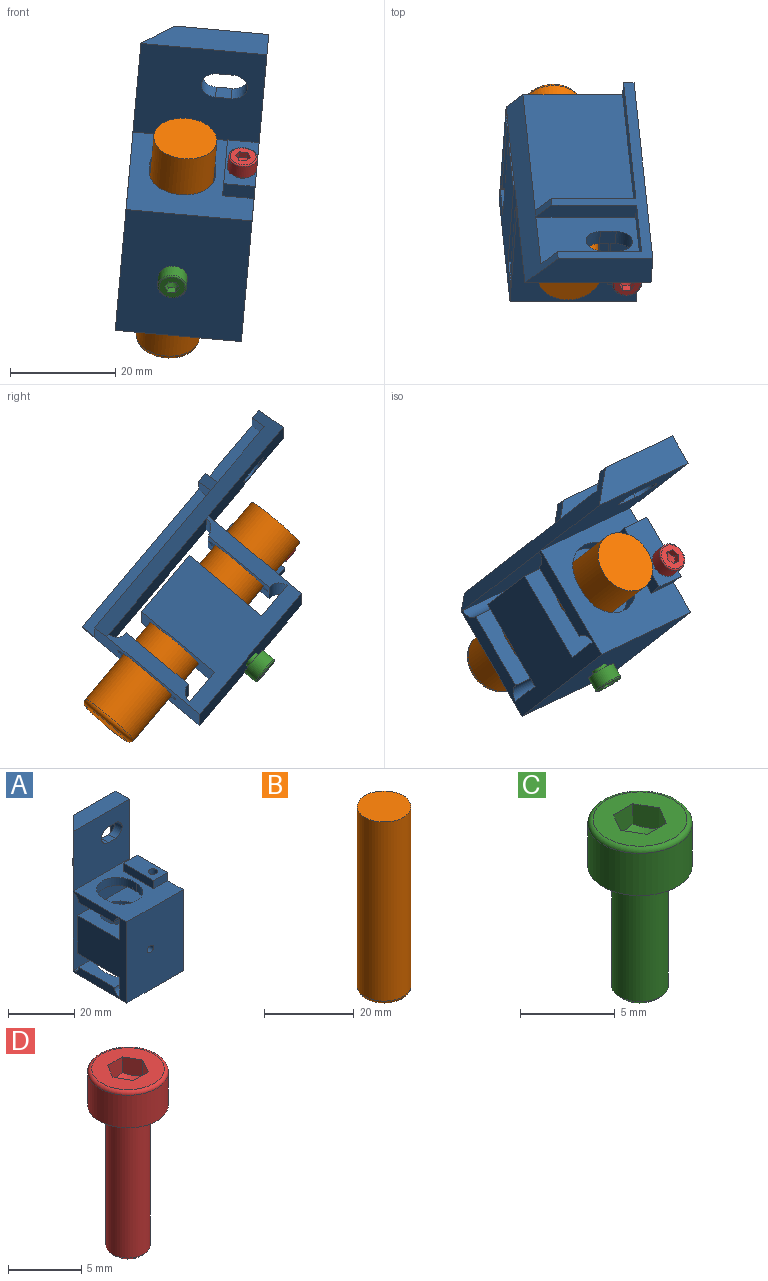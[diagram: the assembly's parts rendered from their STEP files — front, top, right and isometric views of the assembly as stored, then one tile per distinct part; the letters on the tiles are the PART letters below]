
ASSEMBLY  parts=4 mates=3
PART A: 61 faces, bbox 24x29x52 mm
  f0: plane 19x3mm, normal (0,0,-1), area 52.7mm2, adj f1,f11,f48,f58
  f1: plane 34.2x19mm, normal (0,1,0), area 649.8mm2, adj f0,f10,f48,f53
  f2: plane 13.8x3mm, normal (-1,0,0), area 41.4mm2, adj f6,f7,f11,f57
  f3: cylinder r=6.15mm len=3.53mm, axis (0,0,1), area 6.1mm2, adj f4,f46,f54,f59,f60
  f4: plane 9x7.5mm, normal (0,1,0), area 40.4mm2, adj f3,f13,f40,f45,f54,f55,f59
  f5: cylinder r=6.15mm len=14mm, axis (0,0,1), area 479.3mm2, adj f17,f19,f41,f42,f43,f44,f45,f56
  f6: plane 19x13.8mm, normal (0,1,0), area 218.4mm2, adj f2,f7,f49,f50,f51,f52,f53,f57
  f7: plane 19x3mm, normal (0,0,-1), area 52.5mm2, adj f2,f6,f11,f53
  f8: plane 24x6mm, normal (0,0,1), area 126mm2, adj f11,f12,f13,f53
  f9: plane 30x23mm, normal (-1,0,0), area 443.9mm2, adj f10,f14,f15,f16,f17,f18,f19,f20
  f10: plane 29x24mm, normal (0,0,-1), area 475.6mm2, adj f1,f9,f11,f13,f27,f32,f33,f34
  f11: plane 52x18.11mm, normal (0,1,0), area 168.2mm2, adj f0,f2,f7,f8,f10,f13,f48,f53
  f12: plane 24x22mm, normal (0,-1,0), area 484.2mm2, adj f8,f13,f26,f49,f50,f51,f52,f53
  f13: plane 52x29mm, normal (1,0,0), area 755.9mm2, adj f4,f8,f10,f11,f12,f14,f15,f16
  f14: plane 24x15.2mm, normal (0,0,1), area 214.9mm2, adj f9,f13,f15,f25,f32,f33,f34,f35
  f15: cylinder r=2.4mm len=24mm, axis (1,0,0), area 90.5mm2, adj f9,f13,f14,f16
  f16: plane 24x7.33mm, normal (0,1,0), area 175.8mm2, adj f9,f13,f15,f17
  f17: plane 24x18mm, normal (0,0,-1), area 313.2mm2, adj f5,f9,f13,f16,f18
  f18: plane 24x14mm, normal (0,1,0), area 336mm2, adj f9,f13,f17,f19
  f19: plane 24x18mm, normal (0,0,1), area 313.2mm2, adj f5,f9,f13,f18,f20
  f20: plane 24x7.48mm, normal (0,1,0), area 179.4mm2, adj f9,f13,f19,f21
  f21: cylinder r=2.4mm len=24mm, axis (1,0,0), area 90.5mm2, adj f9,f13,f20,f22
  f22: plane 24x15.2mm, normal (0,0,-1), area 208.3mm2, adj f9,f13,f21,f23,f28,f29,f30,f31
  f23: cylinder r=2.4mm len=24mm, axis (1,0,0), area 90.5mm2, adj f9,f13,f22,f24
  f24: plane 28.8x24mm, normal (0,-1,0), area 691.2mm2, adj f13,f23,f25,f53
  f25: cylinder r=2.4mm len=24mm, axis (1,0,0), area 90.5mm2, adj f9,f13,f14,f24
  f26: plane 24x23mm, normal (0,0,1), area 324.1mm2, adj f9,f12,f13,f27,f28,f29,f30,f31
  f27: plane 30x24mm, normal (0,-1,0), area 714.7mm2, adj f9,f10,f13,f26,f56
  f28: cylinder r=6.3mm len=12.6mm, axis (0,0,-1), area 59.4mm2, adj f22,f26,f29,f31
  f29: plane 3x2mm, normal (-1,0,0), area 6mm2, adj f22,f26,f28,f30
  f30: cylinder r=6.3mm len=12.6mm, axis (0,0,-1), area 59.4mm2, adj f22,f26,f29,f31
  f31: plane 3x2mm, normal (1,0,0), area 6mm2, adj f22,f26,f28,f30
  f32: cylinder r=6.3mm len=12.6mm, axis (0,0,1), area 59.4mm2, adj f10,f14,f33,f35
  f33: plane 3x2mm, normal (1,0,0), area 6mm2, adj f10,f14,f32,f34
  f34: cylinder r=6.3mm len=12.6mm, axis (0,0,1), area 59.4mm2, adj f10,f14,f33,f35
  f35: plane 3x2mm, normal (-1,0,0), area 6mm2, adj f10,f14,f32,f34
  f36: plane 13x3mm, normal (-1,0,0), area 39mm2, adj f26,f37,f38,f39
  f37: plane 6x3mm, normal (0,-1,0), area 18mm2, adj f13,f26,f36,f39
  f38: plane 6x3mm, normal (0,1,0), area 18mm2, adj f13,f26,f36,f39
  f39: plane 13x6mm, normal (0,0,1), area 71.4mm2, adj f13,f36,f37,f38,f47
  f40: plane 9x2mm, normal (0,0,-1), area 18mm2, adj f4,f13,f46,f55
  f41: plane 8.63x2.99mm, normal (0,0,-1), area 20.8mm2, adj f5,f13,f42,f46,f60
  f42: plane 9x8.63mm, normal (0,1,0), area 77.7mm2, adj f5,f13,f41,f43
  f43: plane 8.63x6mm, normal (0,0,1), area 48.6mm2, adj f5,f13,f42,f44
  f44: plane 9x8.63mm, normal (0,-1,0), area 77.7mm2, adj f5,f13,f43,f45
  f45: plane 8.63x2.99mm, normal (0,0,-1), area 20.8mm2, adj f4,f5,f13,f44,f59
  f46: plane 9x7.5mm, normal (0,-1,0), area 40.4mm2, adj f3,f13,f40,f41,f54,f55,f60
  f47: cylinder r=1.45mm len=6mm, axis (0,0,1), area 54.7mm2, adj f22,f39
  f48: plane 34.2x3mm, normal (-1,0,0), area 102.6mm2, adj f0,f1,f10,f11
  f49: cylinder r=2.9mm len=5.8mm, axis (0,1,0), area 27.3mm2, adj f6,f12,f50,f52
  f50: plane 3x3mm, normal (0,0,-1), area 9mm2, adj f6,f12,f49,f51
  f51: cylinder r=2.9mm len=5.8mm, axis (0,1,0), area 27.3mm2, adj f6,f12,f50,f52
  f52: plane 3x3mm, normal (0,0,1), area 9mm2, adj f6,f12,f49,f51
  f53: plane 52x6mm, normal (-0.71,0.71,0), area 229.1mm2, adj f1,f6,f7,f8,f9,f10,f11,f12
  f54: plane 2x1.15mm, normal (0,0,1), area 2.2mm2, adj f3,f4,f46,f55
  f55: plane 2x1.46mm, normal (-1,0,0), area 2.9mm2, adj f4,f40,f46,f54
  f56: cylinder r=1.3mm len=6.85mm, axis (0,-1,0), area 56mm2, adj f5,f27
  f57: plane 19x3mm, normal (0,0,1), area 52.7mm2, adj f2,f6,f11,f58
  f58: plane 3x2.89mm, normal (-0.72,0.69,0), area 8.3mm2, adj f0,f11,f53,f57
  f59: bspline ~8.65x4.63mm, area 15.4mm2, adj f3,f4,f5,f45,f60
  f60: bspline ~8.65x4.62mm, area 15.4mm2, adj f3,f5,f41,f46,f59
PART B: 4 faces, bbox 13x13x50 mm
  f0: cylinder r=6mm len=49mm, axis (0,0,-1), area 1847.3mm2, adj f1,f3
  f1: plane 12x12mm, normal (0,0,1), area 113.1mm2, adj f0
  f2: plane 10x10mm, normal (0,0,-1), area 78.5mm2, adj f3
  f3: torus R=5mm, axis (0,0,1), area 55.6mm2, adj f0,f2
PART C: 14 faces, bbox 6x6x11 mm
  f0: cylinder r=2.75mm len=5.5mm, axis (0,0,-1), area 47.1mm2, adj f1,f13
  f1: torus R=2.48mm, axis (0,0,-1), area 7.2mm2, adj f0,f12
  f2: cone r=1.36mm half-angle=45deg, axis (0,0,1), area 3.3mm2, adj f3,f11
  f3: cylinder r=1.5mm len=7.73mm, axis (0,0,-1), area 72.8mm2, adj f2,f13
  f4: cone r=0.72mm half-angle=60deg, axis (0,0,1), area 6.2mm2, adj f5,f6,f7,f8,f9,f10
  f5: plane 1.47x1.25mm, normal (0.87,0.5,0), area 2mm2, adj f4,f6,f10,f12
  f6: plane 1.47x1.44mm, normal (0,1,0), area 2mm2, adj f4,f5,f7,f12
  f7: plane 1.47x1.25mm, normal (-0.87,0.5,0), area 2mm2, adj f4,f6,f8,f12
  f8: plane 1.47x1.25mm, normal (-0.87,-0.5,0), area 2mm2, adj f4,f7,f9,f12
  f9: plane 1.44x1.43mm, normal (0,-1,0), area 2mm2, adj f4,f8,f10,f12
  f10: plane 1.47x1.25mm, normal (0.87,-0.5,0), area 2mm2, adj f4,f5,f9,f12
  f11: plane 2.46x2.46mm, normal (0,0,-1), area 4.7mm2, adj f2
  f12: plane 4.95x4.95mm, normal (0,0,1), area 13.8mm2, adj f1,f5,f6,f7,f8,f9,f10
  f13: plane 5.5x5.5mm, normal (0,0,-1), area 16.7mm2, adj f0,f3
PART D: 14 faces, bbox 6x6x15 mm
  f0: cylinder r=2.75mm len=5.5mm, axis (0,0,-1), area 47.1mm2, adj f1,f13
  f1: torus R=2.48mm, axis (0,0,-1), area 7.2mm2, adj f0,f12
  f2: cone r=1.36mm half-angle=45deg, axis (0,0,1), area 3.3mm2, adj f3,f11
  f3: cylinder r=1.5mm len=11.73mm, axis (0,0,-1), area 110.5mm2, adj f2,f13
  f4: cone r=0.72mm half-angle=60deg, axis (0,0,1), area 6.2mm2, adj f5,f6,f7,f8,f9,f10
  f5: plane 1.47x1.25mm, normal (0.87,0.5,0), area 2mm2, adj f4,f6,f10,f12
  f6: plane 1.47x1.44mm, normal (0,1,0), area 2mm2, adj f4,f5,f7,f12
  f7: plane 1.47x1.25mm, normal (-0.87,0.5,0), area 2mm2, adj f4,f6,f8,f12
  f8: plane 1.47x1.25mm, normal (-0.87,-0.5,0), area 2mm2, adj f4,f7,f9,f12
  f9: plane 1.44x1.43mm, normal (0,-1,0), area 2mm2, adj f4,f8,f10,f12
  f10: plane 1.47x1.25mm, normal (0.87,-0.5,0), area 2mm2, adj f4,f5,f9,f12
  f11: plane 2.46x2.46mm, normal (0,0,-1), area 4.7mm2, adj f2
  f12: plane 4.95x4.95mm, normal (0,0,1), area 13.8mm2, adj f1,f5,f6,f7,f8,f9,f10
  f13: plane 5.5x5.5mm, normal (0,0,-1), area 16.7mm2, adj f0,f3
PLACE A rot(axis=(0.99,0.12,-0.04),40.3deg) t=(21.64,47.01,-26.28)mm
PLACE B rot(axis=(0.99,0.12,-0.04),40.3deg) t=(6.13,44.81,-42.57)mm
PLACE C rot(axis=(1,0.02,-0.04),130.1deg) t=(7.19,16.88,-30.71)mm
PLACE D rot(axis=(0.99,0.12,-0.04),40.3deg) t=(20.28,12.82,-10.09)mm
MATE slider D.f4 <-> A.f47  axis (-0.07,0.64,-0.76) through (19.46,20.54,-19.24)mm
MATE slider C.f4 <-> A.f56  axis (0.06,0.77,0.64) through (7.19,16.88,-30.71)mm
MATE slider B.f0 <-> A.f3  axis (-0.07,0.64,-0.76) through (6.13,44.81,-42.57)mm
